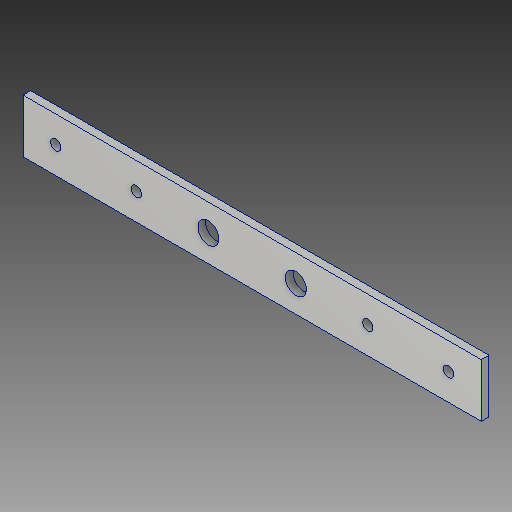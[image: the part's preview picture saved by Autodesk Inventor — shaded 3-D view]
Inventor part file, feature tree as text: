
AUTODESK INVENTOR PART (.ipt)
format: ipt  version: 2017 (Build 210142000, 142)  size: 118,272 bytes
history: native  units: mm
features: extrude x1, sketch x1
ambient origin geometry x8: Origin, YZ Plane, XZ Plane, XY Plane, X Axis, Y Axis, Z Axis, Center Point
bodies: Solid1 (feature_tree)
feature tree (2):
  extrude  "Extrusion1"  Depth=9.525mm TaperAngle=0.0deg
  sketch  "Sketch2"  dims[d25=12.7mm d26=12.7mm d27=26.0mm d28=12.7mm d29=12.7mm d30=26.0mm d31=568.96mm d32=40.64mm d33=140.776mm d34=230.152mm d35=230.152mm d36=40.64mm d37=140.776mm d38=66.305mm d39=33.1525mm d40=33.1525mm d41=33.1525mm d42=33.1525mm d43=33.1525mm d44=33.1525mm d50=9.525mm d51=0.0mm]
